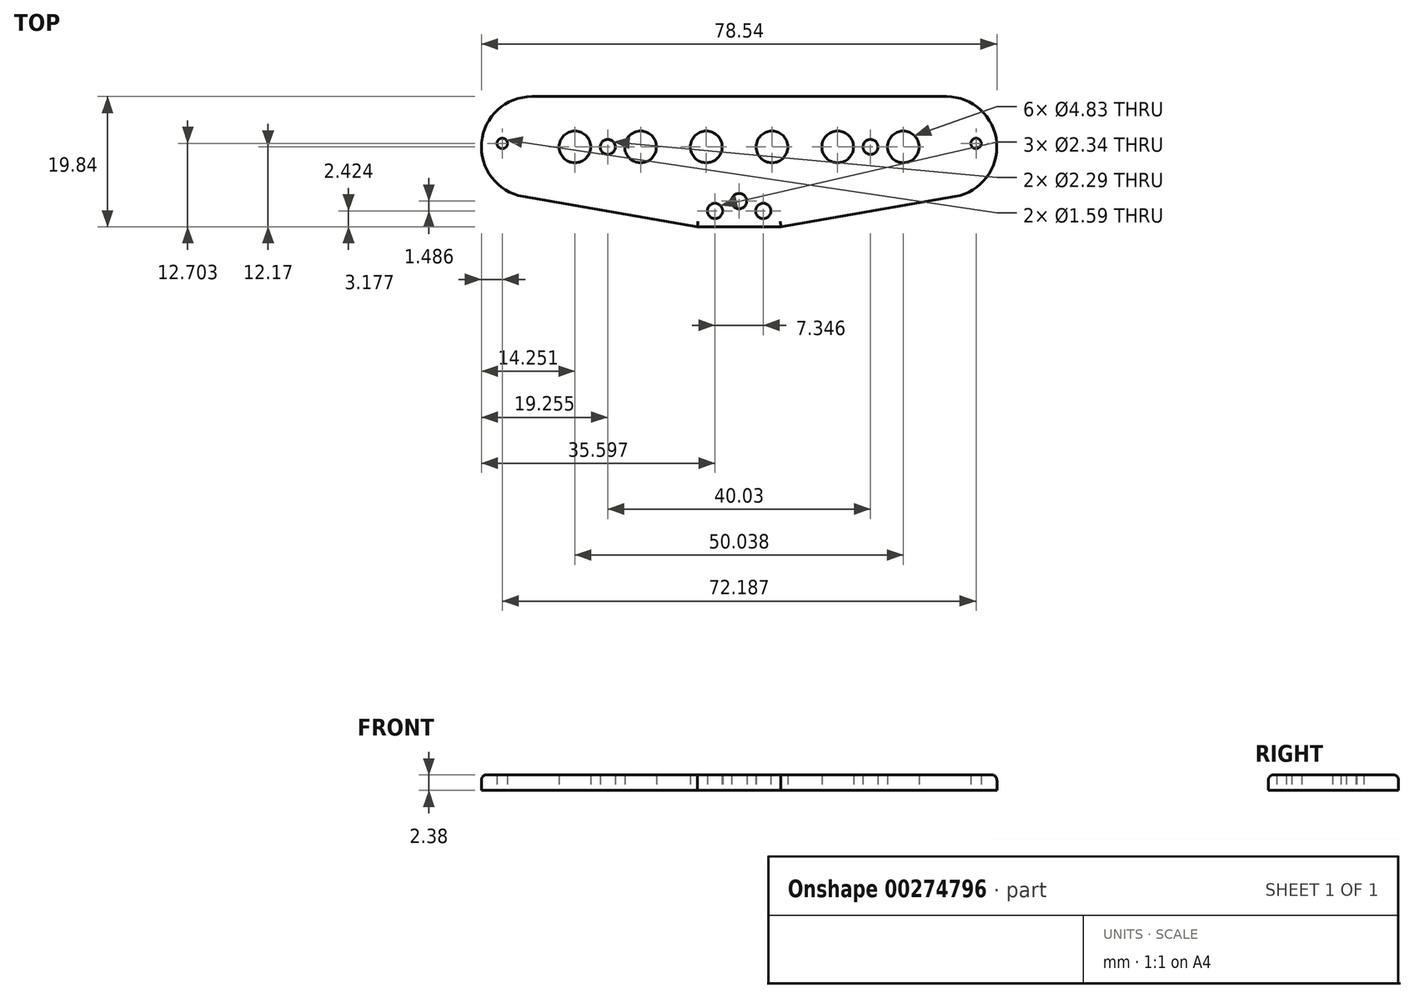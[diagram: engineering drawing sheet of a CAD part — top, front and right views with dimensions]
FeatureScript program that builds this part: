
annotation { "Feature Type Name" : "Feature", "Feature Type Description" : "" }
export const myFeature = defineFeature(function(context is Context, id is Id, definition is map)
    precondition{}
    {
        {
            var Q0;
            Q0=qCreatedBy(makeId("Top.planeOp"),FACE);
            var sketch = newSketch(context, id + "F0", { "sketchPlane" : qUnion([Q0])});
            skCircle(sketch, "E0", {"center": v(5, 0) * mm, "radius": 2.41 * mm});
            skCircle(sketch, "E1.1.0.0", {"center": v(15.01, 0) * mm, "radius": 2.41 * mm});
            skCircle(sketch, "E1.2.0.0", {"center": v(25.02, 0) * mm, "radius": 2.41 * mm});
            skLineSegment(sketch, "E1.direction1", {"start": v(5, 0) * mm, "end": v(15.01, 0) * mm, "construction": true});
            skLineSegment(sketch, "E2", {"start": v(0, 7.67) * mm, "end": v(31.6, 7.67) * mm});
            skArc(sketch, "E3", {"start": v(32.9, -7.56) * mm, "mid": v(39.24, 0.66) * mm, "end": v(31.6, 7.67) * mm});
            skPoint(sketch, "E4", {"position": v(39.27, 0) * mm});
            skLineSegment(sketch, "E5", {"start": v(6.35, -12.17) * mm, "end": v(32.9, -7.56) * mm});
            skCircle(sketch, "E6", {"center": v(36.1, 0.53) * mm, "radius": 0.8 * mm});
            skLineSegment(sketch, "E7.MirrorCS", {"start": v(0, 7.67) * mm, "end": v(-31.6, 7.67) * mm});
            skArc(sketch, "E8.MirrorCS", {"start": v(-32.9, -7.56) * mm, "mid": v(-39.24, 0.66) * mm, "end": v(-31.6, 7.67) * mm});
            skLineSegment(sketch, "E9.MirrorCS", {"start": v(-6.35, -12.17) * mm, "end": v(-32.9, -7.56) * mm});
            skCircle(sketch, "E10.MirrorC", {"center": v(-36.1, 0.53) * mm, "radius": 0.8 * mm});
            skLineSegment(sketch, "E11", {"start": v(-6.35, -12.17) * mm, "end": v(6.35, -12.17) * mm});
            skCircle(sketch, "E12.MirrorC", {"center": v(-5, 0) * mm, "radius": 2.41 * mm});
            skCircle(sketch, "E13.MirrorC", {"center": v(-15.01, 0) * mm, "radius": 2.41 * mm});
            skCircle(sketch, "E14.MirrorC", {"center": v(-25.02, 0) * mm, "radius": 2.41 * mm});
            skCircle(sketch, "E15", {"center": v(0, -8.26) * mm, "radius": 1.17 * mm});
            skCircle(sketch, "E16", {"center": v(3.67, -9.75) * mm, "radius": 1.17 * mm});
            skCircle(sketch, "E17.MirrorC", {"center": v(-3.67, -9.75) * mm, "radius": 1.17 * mm});
            skCircle(sketch, "E18", {"center": v(20.02, 0) * mm, "radius": 1.14 * mm});
            skCircle(sketch, "E19.MirrorC", {"center": v(-20.02, 0) * mm, "radius": 1.14 * mm});
            skSolve(sketch);
        }
        {
            var Q0;
            Q0 = qSketchRegion(id + "F0", true);
            extrude(context, id + "F1", {"entities" : qUnion([Q0]), "depth" : 2.38 * mm});
        }
        {
            var Q0;
            Q0=makeQuery(id+"F1.opExtrude","CAP_EDGE",EDGE,{"disambiguationData":[OSD([sQuery(id+"F0.wireOp",EDGE,"E8.MirrorCS")])],"isStart":false});
            var Q1;
            Q1=makeQuery(id+"F1.opExtrude","CAP_EDGE",EDGE,{"disambiguationData":[OSD([sQuery(id+"F0.wireOp",EDGE,"E9.MirrorCS")])],"isStart":false});
            var Q2;
            Q2=makeQuery(id+"F1.opExtrude","CAP_EDGE",EDGE,{"disambiguationData":[OSD([sQuery(id+"F0.wireOp",EDGE,"E11")])],"isStart":false});
            fillet(context, id + "F2", {"entities" : qUnion([Q0, Q1, Q2]), "radius" : 0.81 * mm, "tangentPropagation" : true, "allowEdgeOverflow" : false});
        }
    });
